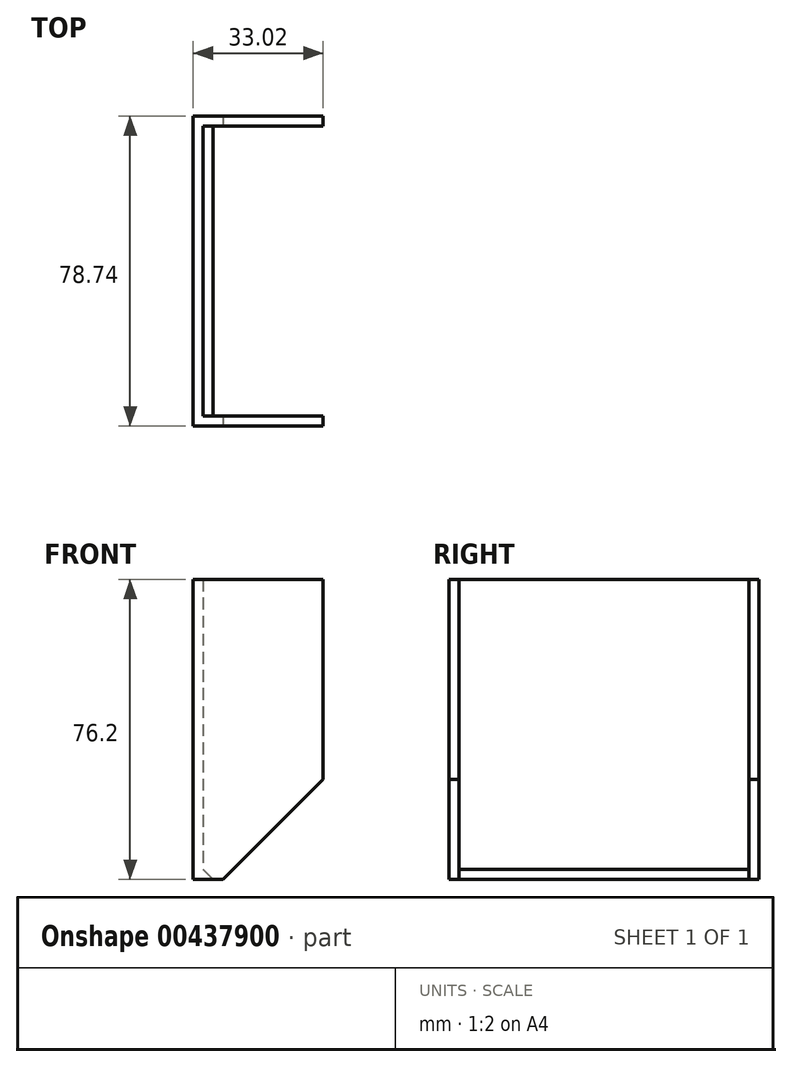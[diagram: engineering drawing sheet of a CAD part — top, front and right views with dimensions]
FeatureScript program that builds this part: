
annotation { "Feature Type Name" : "Feature", "Feature Type Description" : "" }
export const myFeature = defineFeature(function(context is Context, id is Id, definition is map)
    precondition{}
    {
        {
            var Q0;
            Q0=qCreatedBy(makeId("Right.planeOp"),FACE);
            var sketch = newSketch(context, id + "F0", { "sketchPlane" : qUnion([Q0])});
            skLineSegment(sketch, "E0.bottom", {"start": v(-40.83, 25.87) * mm, "end": v(37.91, 25.87) * mm});
            skLineSegment(sketch, "E0.top", {"start": v(-40.83, -50.33) * mm, "end": v(37.91, -50.33) * mm});
            skLineSegment(sketch, "E0.left", {"start": v(-40.83, 25.87) * mm, "end": v(-40.83, -50.33) * mm});
            skLineSegment(sketch, "E0.right", {"start": v(37.91, 25.87) * mm, "end": v(37.91, -50.33) * mm});
            skSolve(sketch);
        }
        {
            var Q0;
            Q0=makeQuery(id+"F0.imprint","IMPRINT",FACE,{"disambiguationData":[TD([[makeQuery(id+"F0.imprint","IMPRINT",EDGE,{"derivedFrom":sQuery(id+"F0.wireOp",EDGE,"E0.bottom")}),-1.0]])]});
            extrude(context, id + "F1", {"entities" : qUnion([Q0]), "depth" : 33.02 * mm});
        }
        {
            var Q0;
            Q0=makeQuery(id+"F1.opExtrude","CAP_FACE",FACE,{"disambiguationData":[OSD([sQuery(id+"F0.wireOp",EDGE,"E0.bottom"),sQuery(id+"F0.wireOp",EDGE,"E0.top"),sQuery(id+"F0.wireOp",EDGE,"E0.left"),sQuery(id+"F0.wireOp",EDGE,"E0.right")])],"isStart":false});
            var Q1;
            Q1=makeQuery(id+"F1.opExtrude","SWEPT_FACE",FACE,{"disambiguationData":[OSD([sQuery(id+"F0.wireOp",EDGE,"E0.bottom")])]});
            shell(context, id + "F2", {"entities" : qUnion([Q0, Q1]), "thickness" : 2.54 * mm});
        }
        {
            var Q0;
            {var subQ0=sQuery(id+"F0.wireOp",EDGE,"E0.top");Q0=makeQuery(id+"F2.opShell","OFFSET_EDGE",EDGE,{"disambiguationData":[OSD([subQ0]),TDD([makeQuery(id+"F1.opExtrude","CAP_EDGE",EDGE,{"disambiguationData":[OSD([subQ0])],"isStart":false})])]});}
            chamfer(context, id + "F3", {"entities" : qUnion([Q0]), "width" : 30.48 * mm, "tangentPropagation" : true});
        }
        {
            var Q0;
            Q0=makeQuery(id+"F1.opExtrude","CAP_EDGE",EDGE,{"disambiguationData":[OSD([sQuery(id+"F0.wireOp",EDGE,"E0.top")])],"isStart":false});
            chamfer(context, id + "F4", {"entities" : qUnion([Q0]), "width" : 25.4 * mm, "tangentPropagation" : true});
        }
    });
